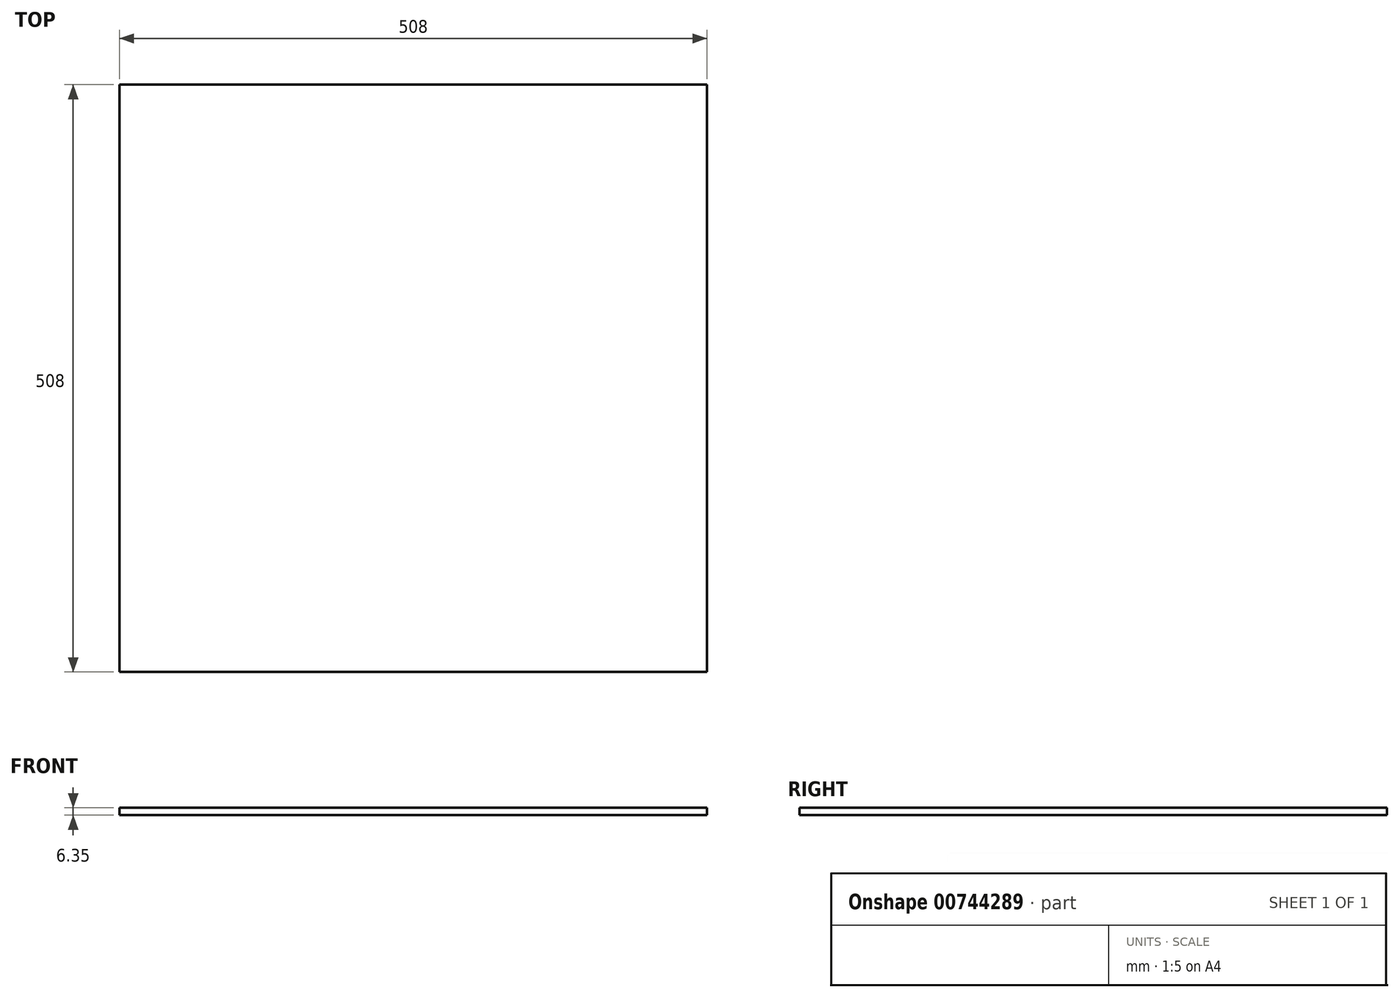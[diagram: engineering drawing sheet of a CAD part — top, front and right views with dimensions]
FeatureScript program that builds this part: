
annotation { "Feature Type Name" : "Feature", "Feature Type Description" : "" }
export const myFeature = defineFeature(function(context is Context, id is Id, definition is map)
    precondition{}
    {
        {
            var Q0;
            Q0=qCreatedBy(makeId("Top.planeOp"),FACE);
            var sketch = newSketch(context, id + "F0", { "sketchPlane" : qUnion([Q0])});
            skLineSegment(sketch, "E0.bottom", {"start": v(-272.82, -248.95) * mm, "end": v(235.18, -248.95) * mm});
            skLineSegment(sketch, "E0.top", {"start": v(-272.82, 259.05) * mm, "end": v(235.18, 259.05) * mm});
            skLineSegment(sketch, "E0.left", {"start": v(-272.82, -248.95) * mm, "end": v(-272.82, 259.05) * mm});
            skLineSegment(sketch, "E0.right", {"start": v(235.18, -248.95) * mm, "end": v(235.18, 259.05) * mm});
            skSolve(sketch);
        }
        {
            var Q0;
            Q0 = qSketchRegion(id + "F0", true);
            extrude(context, id + "F1", {"entities" : qUnion([Q0]), "depth" : 6.35 * mm, "offsetDistance" : 25.4 * mm});
        }
    });
